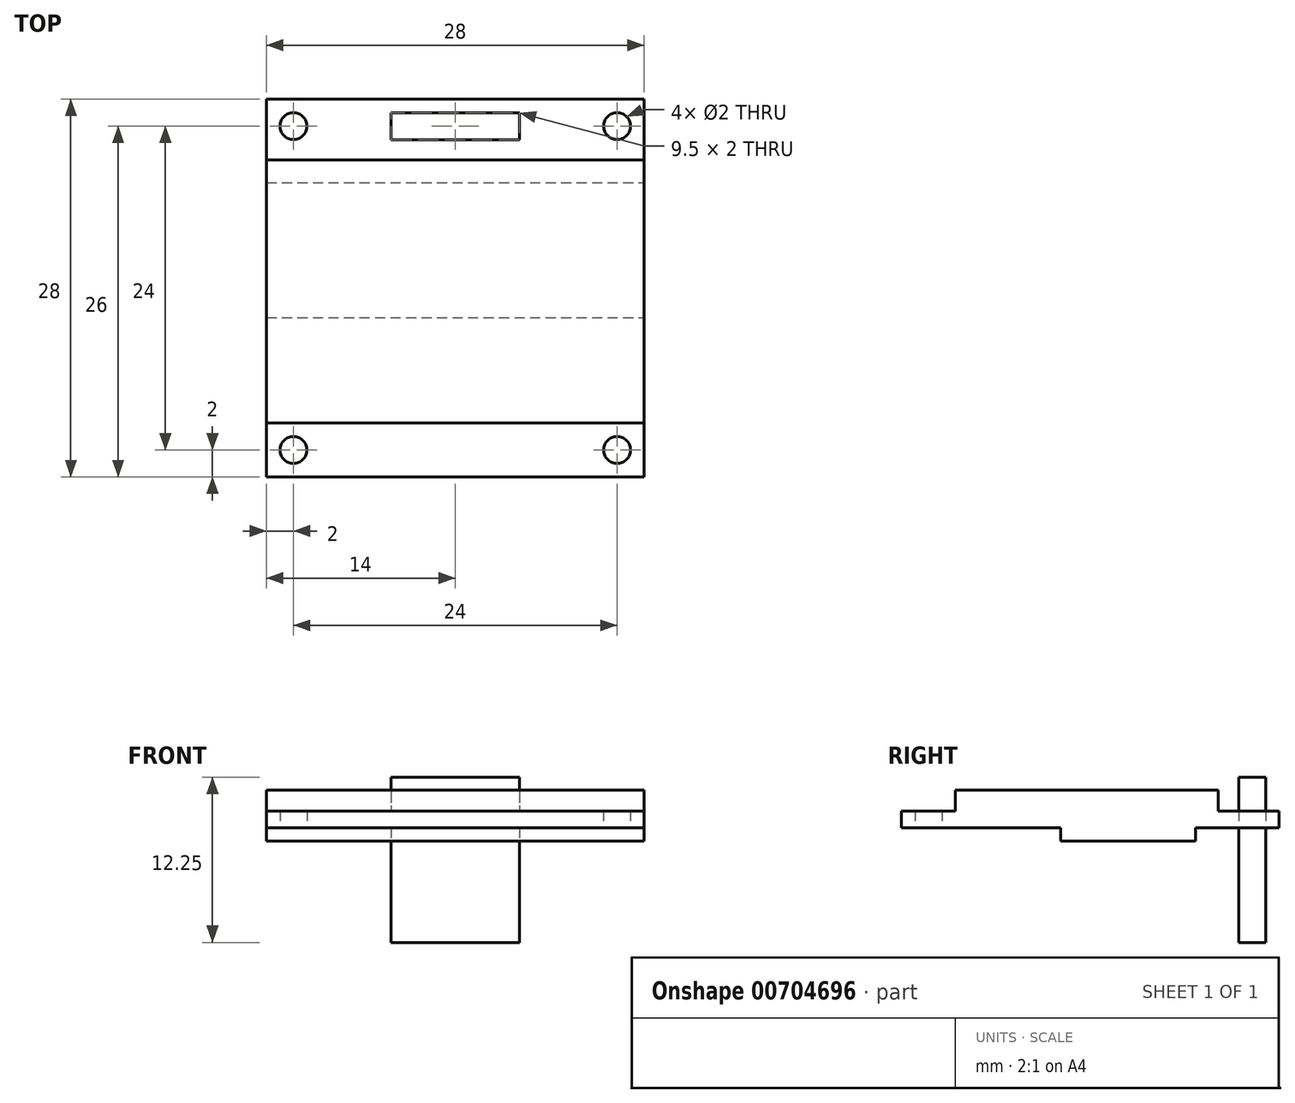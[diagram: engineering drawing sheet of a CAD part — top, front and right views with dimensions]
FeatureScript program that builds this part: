
annotation { "Feature Type Name" : "Feature", "Feature Type Description" : "" }
export const myFeature = defineFeature(function(context is Context, id is Id, definition is map)
    precondition{}
    {
        {
            var Q0;
            Q0=qCreatedBy(makeId("Top.planeOp"),FACE);
            var sketch = newSketch(context, id + "F0", { "sketchPlane" : qUnion([Q0])});
            skLineSegment(sketch, "E0.bottom", {"start": v(-14, 14) * mm, "end": v(14, 14) * mm});
            skLineSegment(sketch, "E0.top", {"start": v(-14, -14) * mm, "end": v(14, -14) * mm});
            skLineSegment(sketch, "E0.left", {"start": v(-14, 14) * mm, "end": v(-14, -14) * mm});
            skLineSegment(sketch, "E0.right", {"start": v(14, 14) * mm, "end": v(14, -14) * mm});
            skCircle(sketch, "E1", {"center": v(12, 12) * mm, "radius": 1 * mm});
            skCircle(sketch, "E2", {"center": v(12, -12) * mm, "radius": 1 * mm});
            skCircle(sketch, "E3", {"center": v(-12, -12) * mm, "radius": 1 * mm});
            skCircle(sketch, "E4", {"center": v(-12, 12) * mm, "radius": 1 * mm});
            skLineSegment(sketch, "E5.bottom", {"start": v(-14, 9.5) * mm, "end": v(14, 9.5) * mm});
            skLineSegment(sketch, "E5.top", {"start": v(-14, -10) * mm, "end": v(14, -10) * mm});
            skLineSegment(sketch, "E5.left", {"start": v(-14, 9.5) * mm, "end": v(-14, -10) * mm});
            skLineSegment(sketch, "E5.right", {"start": v(14, 9.5) * mm, "end": v(14, -10) * mm});
            skLineSegment(sketch, "E6.bottom", {"start": v(-4.75, 13) * mm, "end": v(4.75, 13) * mm});
            skLineSegment(sketch, "E6.top", {"start": v(-4.75, 11) * mm, "end": v(4.75, 11) * mm});
            skLineSegment(sketch, "E6.left", {"start": v(-4.75, 13) * mm, "end": v(-4.75, 11) * mm});
            skLineSegment(sketch, "E6.right", {"start": v(4.75, 13) * mm, "end": v(4.75, 11) * mm});
            skLineSegment(sketch, "E7.bottom", {"start": v(-14, 7.82) * mm, "end": v(14, 7.82) * mm});
            skLineSegment(sketch, "E7.top", {"start": v(-14, -2.18) * mm, "end": v(14, -2.18) * mm});
            skLineSegment(sketch, "E7.left", {"start": v(-14, 7.82) * mm, "end": v(-14, -2.18) * mm});
            skLineSegment(sketch, "E7.right", {"start": v(14, 7.82) * mm, "end": v(14, -2.18) * mm});
            skSolve(sketch);
        }
        {
            var Q0;
            {var subQ1=sQuery(id+"F0.wireOp",EDGE,"E0.bottom");Q0=makeQuery(id+"F0.imprint","IMPRINT",FACE,{"disambiguationData":[TD([[makeQuery(id+"F0.imprint","IMPRINT",EDGE,{"derivedFrom":subQ1}),-1.0]])]});}
            var Q1;
            Q1=makeQuery(id+"F0.imprint","IMPRINT",FACE,{"disambiguationData":[TD([[makeQuery(id+"F0.imprint","IMPRINT",EDGE,{"derivedFrom":sQuery(id+"F0.wireOp",EDGE,"E6.bottom")}),-1.0]])]});
            var Q2;
            Q2=makeQuery(id+"F0.imprint","IMPRINT",FACE,{"disambiguationData":[TD([[makeQuery(id+"F0.imprint","IMPRINT",EDGE,{"derivedFrom":sQuery(id+"F0.wireOp",EDGE,"E5.bottom")}),-1.0]])]});
            var Q3;
            {var subQ1=sQuery(id+"F0.wireOp",EDGE,"E0.top");Q3=makeQuery(id+"F0.imprint","IMPRINT",FACE,{"disambiguationData":[TD([[makeQuery(id+"F0.imprint","IMPRINT",EDGE,{"derivedFrom":subQ1}),1.0]])]});}
            var Q4;
            Q4=makeQuery(id+"F0.imprint","IMPRINT",FACE,{"disambiguationData":[TD([[makeQuery(id+"F0.imprint","IMPRINT",EDGE,{"derivedFrom":sQuery(id+"F0.wireOp",EDGE,"E7.bottom")}),-1.0]])]});
            var Q5;
            {var subQ0=sQuery(id+"F0.wireOp",EDGE,"E5.top");Q5=makeQuery(id+"F0.imprint","IMPRINT",FACE,{"disambiguationData":[TD([[makeQuery(id+"F0.imprint","IMPRINT",EDGE,{"derivedFrom":subQ0}),1.0]])]});}
            extrude(context, id + "F1", {"entities" : qUnion([Q0, Q1, Q2, Q3, Q4, Q5]), "depth" : 1.25 * mm, "offsetDistance" : 25 * mm});
        }
        {
            var Q0;
            Q0=makeQuery(id+"F0.imprint","IMPRINT",FACE,{"disambiguationData":[TD([[makeQuery(id+"F0.imprint","IMPRINT",EDGE,{"derivedFrom":sQuery(id+"F0.wireOp",EDGE,"E6.bottom")}),-1.0]])]});
            extrude(context, id + "F2", {"entities" : qUnion([Q0]), "operationType" : NewBodyOperationType.ADD, "depth" : 3.75 * mm, "offsetDistance" : 25 * mm, "hasSecondDirection" : true, "secondDirectionOppositeDirection" : true, "secondDirectionDepth" : 8.5 * mm});
        }
        {
            var Q0;
            Q0=makeQuery(id+"F0.imprint","IMPRINT",FACE,{"disambiguationData":[TD([[makeQuery(id+"F0.imprint","IMPRINT",EDGE,{"derivedFrom":sQuery(id+"F0.wireOp",EDGE,"E7.bottom")}),-1.0]])]});
            extrude(context, id + "F3", {"entities" : qUnion([Q0]), "operationType" : NewBodyOperationType.ADD, "oppositeDirection" : true, "depth" : 1 * mm, "offsetDistance" : 25 * mm});
        }
        {
            var Q0;
            Q0=makeQuery(id+"F0.imprint","IMPRINT",FACE,{"disambiguationData":[TD([[makeQuery(id+"F0.imprint","IMPRINT",EDGE,{"derivedFrom":sQuery(id+"F0.wireOp",EDGE,"E7.bottom")}),-1.0]])]});
            var Q1;
            {var subQ0=sQuery(id+"F0.wireOp",EDGE,"E5.top");Q1=makeQuery(id+"F0.imprint","IMPRINT",FACE,{"disambiguationData":[TD([[makeQuery(id+"F0.imprint","IMPRINT",EDGE,{"derivedFrom":subQ0}),1.0]])]});}
            var Q2;
            {var subQ0=sQuery(id+"F0.wireOp",EDGE,"E5.bottom");Q2=makeQuery(id+"F0.imprint","IMPRINT",FACE,{"disambiguationData":[TD([[makeQuery(id+"F0.imprint","IMPRINT",EDGE,{"derivedFrom":subQ0}),-1.0]])]});}
            extrude(context, id + "F4", {"entities" : qUnion([Q0, Q1, Q2]), "operationType" : NewBodyOperationType.ADD, "depth" : 2.8 * mm, "offsetDistance" : 25 * mm});
        }
    });
